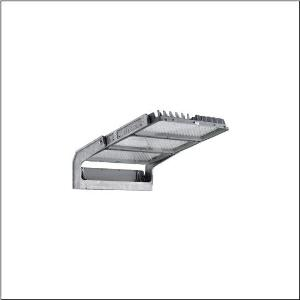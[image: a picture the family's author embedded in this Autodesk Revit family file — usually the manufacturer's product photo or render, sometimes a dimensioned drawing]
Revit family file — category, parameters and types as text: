
# Revit family: floodlight_fl_11_maxi_pro_remote___rs07_5xa779224k01gb_72aa
name_source: partatom
category: Lighting Fixtures
units: mm (PartAtom-declared; Revit-internal decimal feet)

## family parameters
Cut with Voids When Loaded = No
Host = Face
Light Source = No
Part Type = Normal
Room Calculation Point = No
Round Connector Dimension = Use Diameter
Shared = No

## types (1)
- --- (1 x LED, 123000 lm, 1227.1 W, 5700K)
    Apparent Load = 1227 VA
    CIE Flux Codes = 80 93 99 100 99
    Color Rendering = 90
    Color Temperature = 5700K
    Default Elevation = 1800 mm
    Description = Floodlight FL 11  maxi  pro Remote floodlight; light control with lens of PMMA; cover panel of toughened safety glass, transparent; light distribution: RS07, rotationally symmetric direct distribution, LED; colour temperature: 5700K, rated luminous flux: 123.000lm, colour rendering: CRI > 90, light colour: 957; luminous efficacy: 100lm/W; brightness control: DMX+RDM; with terminal, 8-pole, max. 2.5mm², mains connection: 220..240V/380..400V AC, 50/60Hz, surge voltage resistance: line to ground: 10kV, LED service life up to 100,000h L90. Typical operating time: 1000h per year., ECG replaceable separately, LED unit replaceable without ESD environment, dustproof LED module, dimming range 10..100%; 1227W floodlight with 3x LED unit of diecast aluminium, coated grey; length: 1.003mm / width: 651mm / height: 338mm; mounting bracket, of diecast aluminium, uncoated, natural, equipment: Power, protection rating (complete): IP66; insulation class (complete): insulation class I (protective earthing); certification: CE, ENEC, VDE; ball protection: ball impact resistant, only for outdoor installations in the designated locations, permissible operating ambient temperature: -45..+55°C, permissible storage temperature: -40..+85°Cpackaging unit: 1 piece

Light Distribution: RS07
    Height = 320 mm
    Lamp = 1 x LED
    Lamp Light Flux = 123000 lm
    Lamp Power = 1227.1 W
    Lamp count = 1
    Length = 1002 mm
    Luminous efficacy = 100 lm/W
    Manufacturer = Siteco
    ModVariant = No
    Model = 5XA779224K01GB
    Mounting Place = Ceiling
    Mounting Type = Surface mounted
    Number of Poles = 1
    OnlyDefault = Yes
    Power Factor = 1
    Product Name = Floodlight FL 11 maxi pro Remote | RS07
    Product group = floodlight | ceiling mounted
    ProductGroupID = 303
    Protection Class = Protection class I
    Protection Degree = IP 66
    RLX_Detail_Level = 1
    RLX_Emergency_Light_Flux = 0 lm
    RLX_Emergency_Type = 0
    RLX_Emergency_Type_DB = No
    RlxData = <blob elided: 40269 chars, md5=d1e48a17>
    Socket = socket
    Standby Power = 0 W
    System Light Flux = 123000 lm
    System Power = 1227 W
    Type Comments = factory setting: luminous flux: 100 % | dim-lin: 255 | 840 mA
    Type Image = l_1356210.jpg
    URL = http://relux.com
    VarID = @adj_033425
    Voltage = 0 V
    Weight = 0.00 kg
    Width = 655 mm

## geometry (parser evidence)
native form markers: Blend x4, Sweep x13
no freeform markers — native parametric forms only
